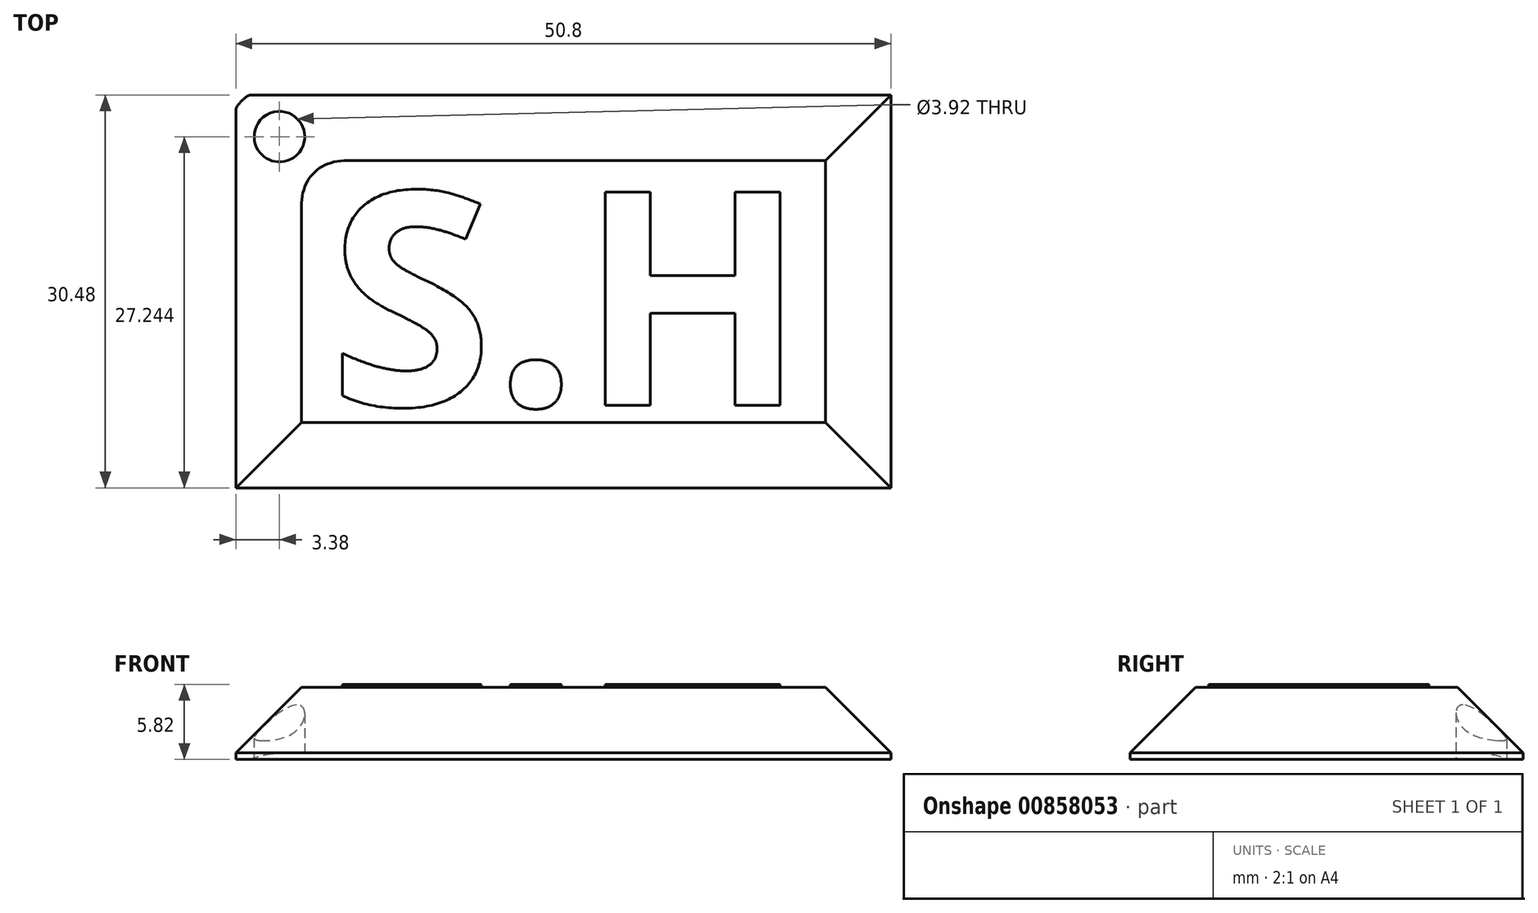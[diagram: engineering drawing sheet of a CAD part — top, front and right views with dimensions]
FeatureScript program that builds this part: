
annotation { "Feature Type Name" : "Feature", "Feature Type Description" : "" }
export const myFeature = defineFeature(function(context is Context, id is Id, definition is map)
    precondition{}
    {
        {
            var Q0;
            Q0=qCreatedBy(makeId("Top.planeOp"),FACE);
            var sketch = newSketch(context, id + "F0", { "sketchPlane" : qUnion([Q0])});
            skLineSegment(sketch, "E0.bottom", {"start": v(0, 0) * mm, "end": v(50.8, 0) * mm});
            skLineSegment(sketch, "E0.top", {"start": v(0, 30.48) * mm, "end": v(50.8, 30.48) * mm});
            skLineSegment(sketch, "E0.left", {"start": v(0, 0) * mm, "end": v(0, 30.48) * mm});
            skLineSegment(sketch, "E0.right", {"start": v(50.8, 0) * mm, "end": v(50.8, 30.48) * mm});
            skSolve(sketch);
        }
        {
            var Q0;
            Q0 = qSketchRegion(id + "F0", true);
            extrude(context, id + "F1", {"entities" : qUnion([Q0]), "depth" : 5.6 * mm, "offsetDistance" : 25.4 * mm});
        }
        {
            var Q0;
            Q0=makeQuery(id+"F1.opExtrude","CAP_EDGE",EDGE,{"disambiguationData":[OSD([sQuery(id+"F0.wireOp",EDGE,"E0.left")])],"isStart":false});
            var Q1;
            Q1=makeQuery(id+"F1.opExtrude","CAP_EDGE",EDGE,{"disambiguationData":[OSD([sQuery(id+"F0.wireOp",EDGE,"E0.top")])],"isStart":false});
            var Q2;
            Q2=makeQuery(id+"F1.opExtrude","CAP_EDGE",EDGE,{"disambiguationData":[OSD([sQuery(id+"F0.wireOp",EDGE,"E0.right")])],"isStart":false});
            var Q3;
            Q3=makeQuery(id+"F1.opExtrude","CAP_EDGE",EDGE,{"disambiguationData":[OSD([sQuery(id+"F0.wireOp",EDGE,"E0.bottom")])],"isStart":false});
            chamfer(context, id + "F2", {"entities" : qUnion([Q0, Q1, Q2, Q3]), "width" : 5.08 * mm, "tangentPropagation" : true});
        }
        {
            var Q0;
            Q0=qCreatedBy(makeId("Top.planeOp"),FACE);
            var sketch = newSketch(context, id + "F3", { "sketchPlane" : qUnion([Q0])});
            skText(sketch, "E1", { "text": "S.H", "fontName": "OpenSans-Bold.ttf"});
            const initialGuessF3  = {"E1": [0.0072, 0.0064, 1, 0, 0.01668]};
            skSetInitialGuess(sketch, initialGuessF3);
            skSolve(sketch);
        }
        {
            var Q0;
            Q0 = qSketchRegion(id + "F3", true);
            extrude(context, id + "F4", {"entities" : qUnion([Q0]), "operationType" : NewBodyOperationType.ADD, "depth" : 5.82 * mm, "offsetDistance" : 25.4 * mm});
        }
        {
            var Q0;
            Q0=qCreatedBy(makeId("Top.planeOp"),FACE);
            var sketch = newSketch(context, id + "F5", { "sketchPlane" : qUnion([Q0])});
            skCircle(sketch, "E2", {"center": v(3.38, 27.24) * mm, "radius": 1.96 * mm});
            skSolve(sketch);
        }
        {
            var Q0;
            Q0 = qSketchRegion(id + "F5", true);
            extrude(context, id + "F6", {"entities" : qUnion([Q0]), "operationType" : NewBodyOperationType.REMOVE, "depth" : 25.15 * mm, "offsetDistance" : 25.4 * mm});
        }
        {
            var Q0;
            {var subQ0=sQuery(id+"F0.wireOp",EDGE,"E0.top");var subQ1=sQuery(id+"F0.wireOp",EDGE,"E0.left");Q0=makeQuery(id+"F6.boolean.opBoolean","SPLIT",EDGE,{"disambiguationData":[TD([makeQuery(id+"F1.opExtrude","SWEPT_FACE",FACE,{"disambiguationData":[OSD([subQ0])]})])],"derivedFrom":makeQuery(id+"F2.opChamfer","BLEND_EDGE",EDGE,{"blendedFrom":[makeQuery(id+"F1.opExtrude","CAP_EDGE",EDGE,{"disambiguationData":[OSD([subQ0])],"isStart":false}),makeQuery(id+"F1.opExtrude","CAP_EDGE",EDGE,{"disambiguationData":[OSD([subQ1])],"isStart":false})],"blendedInto":[]})});}
            fillet(context, id + "F7", {"entities" : qUnion([Q0]), "radius" : 5.08 * mm, "tangentPropagation" : true, "allowEdgeOverflow" : false});
        }
    });
